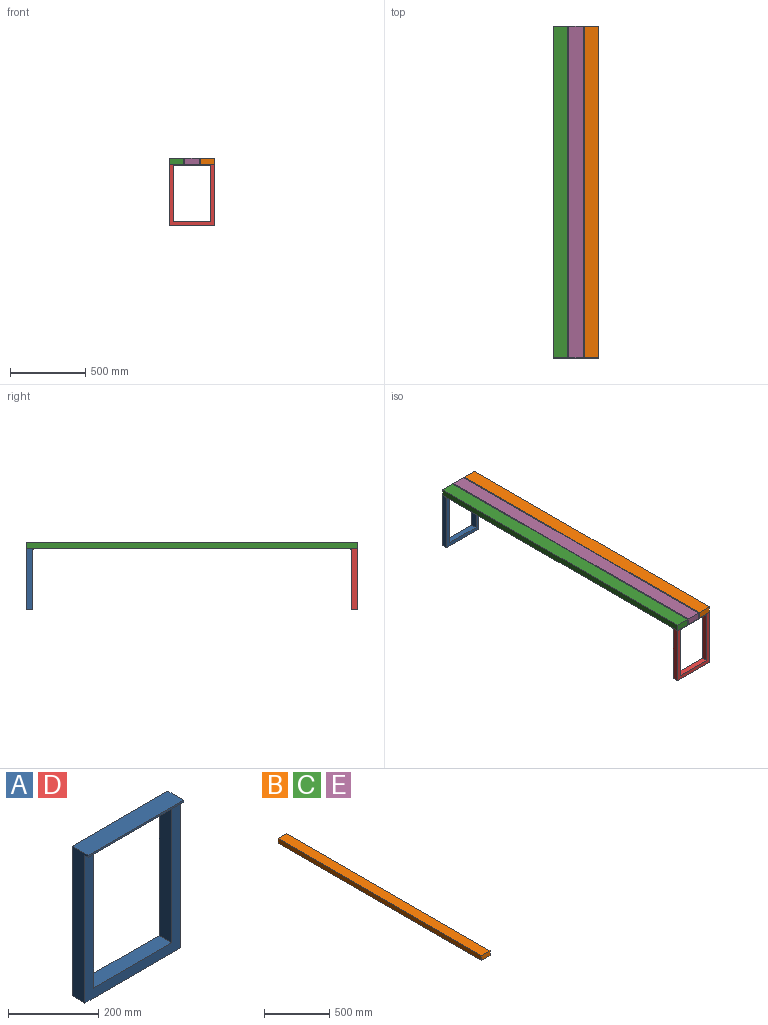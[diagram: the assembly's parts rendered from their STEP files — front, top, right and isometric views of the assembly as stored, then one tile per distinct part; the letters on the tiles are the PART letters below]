
ASSEMBLY  parts=5 mates=2
PART A: 11 faces, bbox 300x50x406 mm
  f0: plane 406x50mm, normal (-1,0,0), area 16290mm2, adj f1,f6,f7,f8,f9,f10
  f1: plane 300x40mm, normal (0,0,-1), area 12000mm2, adj f0,f2,f6,f7
  f2: plane 406x50mm, normal (1,0,0), area 16290mm2, adj f1,f6,f7,f8,f9,f10
  f3: plane 374x40mm, normal (-1,0,0), area 14960mm2, adj f4,f6,f7,f8
  f4: plane 246x40mm, normal (0,0,1), area 9840mm2, adj f3,f5,f6,f7
  f5: plane 374x40mm, normal (1,0,0), area 14960mm2, adj f4,f6,f7,f8
  f6: plane 401x300mm, normal (0,-1,0), area 28296mm2, adj f0,f1,f2,f3,f4,f5,f8
  f7: plane 406x300mm, normal (0,1,0), area 29796mm2, adj f0,f1,f2,f3,f4,f5,f8,f9
  f8: plane 300x50mm, normal (0,0,-1), area 12840mm2, adj f0,f2,f3,f5,f6,f7,f10
  f9: plane 300x50mm, normal (0,0,1), area 15000mm2, adj f0,f2,f7,f10
  f10: plane 300x5mm, normal (0,-1,0), area 1500mm2, adj f0,f2,f8,f9
PART B: 6 faces, bbox 95x2200x44 mm
  f0: plane 2200x95mm, normal (0,0,1), area 209000mm2, adj f1,f3,f4,f5
  f1: plane 2200x44mm, normal (-1,0,0), area 96800mm2, adj f0,f2,f4,f5
  f2: plane 2200x95mm, normal (0,0,-1), area 209000mm2, adj f1,f3,f4,f5
  f3: plane 2200x44mm, normal (1,0,0), area 96800mm2, adj f0,f2,f4,f5
  f4: plane 95x44mm, normal (0,-1,0), area 4180mm2, adj f0,f1,f2,f3
  f5: plane 95x44mm, normal (0,1,0), area 4180mm2, adj f0,f1,f2,f3
PART C: same geometry as B
PART D: same geometry as A
PART E: same geometry as B
PLACE A at identity
PLACE B t=(102.5,0,428)mm
PLACE C t=(-102.5,0,428)mm
PLACE D rot(axis=(0,0,-1),180deg) t=(0,-2200,0)mm
PLACE E t=(0,0,428)mm
MATE fastened D.f2 <-> C.f1  axis (-1,0,0) through (-150,-2200,406)mm
MATE fastened C.f2 <-> A.f9  axis (0,0,1) through (-150,0,406)mm
